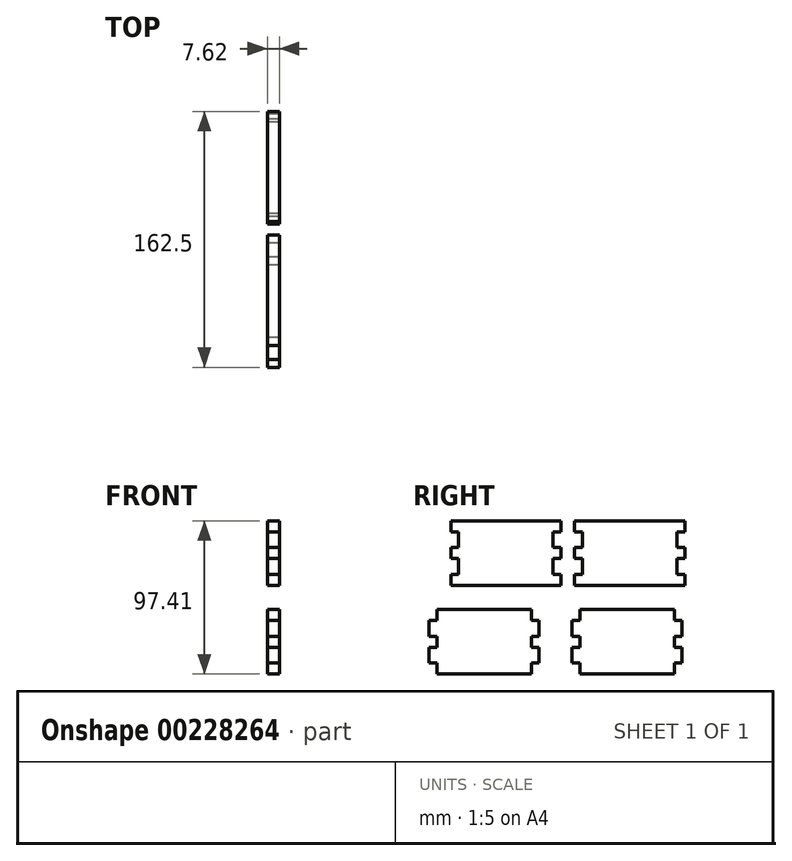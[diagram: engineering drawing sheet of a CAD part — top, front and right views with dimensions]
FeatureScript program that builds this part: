
annotation { "Feature Type Name" : "Feature", "Feature Type Description" : "" }
export const myFeature = defineFeature(function(context is Context, id is Id, definition is map)
    precondition{}
    {
        {
            var Q0;
            Q0=qCreatedBy(makeId("Right.planeOp"),FACE);
            var sketch = newSketch(context, id + "F0", { "sketchPlane" : qUnion([Q0])});
            skLineSegment(sketch, "E0", {"start": v(17.1, 53.44) * mm, "end": v(-52.9, 53.44) * mm});
            skLineSegment(sketch, "E1", {"start": v(-52.9, 53.44) * mm, "end": v(-52.9, 46.44) * mm});
            skLineSegment(sketch, "E2", {"start": v(-52.9, 46.44) * mm, "end": v(-47.9, 46.44) * mm});
            skLineSegment(sketch, "E3", {"start": v(-47.9, 46.44) * mm, "end": v(-47.9, 36.44) * mm});
            skLineSegment(sketch, "E4", {"start": v(-47.9, 36.44) * mm, "end": v(-52.9, 36.44) * mm});
            skLineSegment(sketch, "E5", {"start": v(-52.9, 36.44) * mm, "end": v(-52.9, 29.44) * mm});
            skLineSegment(sketch, "E6", {"start": v(-52.9, 29.44) * mm, "end": v(-47.9, 29.44) * mm});
            skLineSegment(sketch, "E7", {"start": v(-47.9, 29.44) * mm, "end": v(-47.9, 19.44) * mm});
            skLineSegment(sketch, "E8", {"start": v(-47.9, 19.44) * mm, "end": v(-52.9, 19.44) * mm});
            skLineSegment(sketch, "E9", {"start": v(-52.9, 19.44) * mm, "end": v(-52.9, 12.44) * mm});
            skLineSegment(sketch, "E10", {"start": v(-52.9, 12.44) * mm, "end": v(17.1, 12.44) * mm});
            skLineSegment(sketch, "E11", {"start": v(17.1, 12.44) * mm, "end": v(17.1, 19.44) * mm});
            skLineSegment(sketch, "E12", {"start": v(17.1, 19.44) * mm, "end": v(12.1, 19.44) * mm});
            skLineSegment(sketch, "E13", {"start": v(12.1, 19.44) * mm, "end": v(12.1, 29.44) * mm});
            skLineSegment(sketch, "E14", {"start": v(12.1, 29.44) * mm, "end": v(17.1, 29.44) * mm});
            skLineSegment(sketch, "E15", {"start": v(17.1, 29.44) * mm, "end": v(17.1, 36.44) * mm});
            skLineSegment(sketch, "E16", {"start": v(17.1, 36.44) * mm, "end": v(12.1, 36.44) * mm});
            skLineSegment(sketch, "E17", {"start": v(12.1, 36.44) * mm, "end": v(12.1, 46.44) * mm});
            skLineSegment(sketch, "E18", {"start": v(12.1, 46.44) * mm, "end": v(17.1, 46.44) * mm});
            skLineSegment(sketch, "E19", {"start": v(17.1, 46.44) * mm, "end": v(17.1, 53.44) * mm});
            skLineSegment(sketch, "E20.MirrorCS", {"start": v(25.75, 36.44) * mm, "end": v(30.75, 36.44) * mm});
            skLineSegment(sketch, "E21.MirrorCS", {"start": v(95.75, 29.44) * mm, "end": v(90.75, 29.44) * mm});
            skLineSegment(sketch, "E22.MirrorCS", {"start": v(30.75, 46.44) * mm, "end": v(25.75, 46.44) * mm});
            skLineSegment(sketch, "E23.MirrorCS", {"start": v(90.75, 19.44) * mm, "end": v(95.75, 19.44) * mm});
            skLineSegment(sketch, "E24.MirrorCS", {"start": v(95.75, 46.44) * mm, "end": v(90.75, 46.44) * mm});
            skLineSegment(sketch, "E25.MirrorCS", {"start": v(25.75, 19.44) * mm, "end": v(30.75, 19.44) * mm});
            skLineSegment(sketch, "E26.MirrorCS", {"start": v(30.75, 29.44) * mm, "end": v(25.75, 29.44) * mm});
            skLineSegment(sketch, "E27.MirrorCS", {"start": v(90.75, 36.44) * mm, "end": v(95.75, 36.44) * mm});
            skLineSegment(sketch, "E28.MirrorCS", {"start": v(30.75, 19.44) * mm, "end": v(30.75, 29.44) * mm});
            skLineSegment(sketch, "E29.MirrorCS", {"start": v(90.75, 29.44) * mm, "end": v(90.75, 19.44) * mm});
            skLineSegment(sketch, "E30.MirrorCS", {"start": v(95.75, 36.44) * mm, "end": v(95.75, 29.44) * mm});
            skLineSegment(sketch, "E31.MirrorCS", {"start": v(95.75, 19.44) * mm, "end": v(95.75, 12.44) * mm});
            skLineSegment(sketch, "E32.MirrorCS", {"start": v(95.75, 53.44) * mm, "end": v(95.75, 46.44) * mm});
            skLineSegment(sketch, "E33.MirrorCS", {"start": v(95.75, 12.44) * mm, "end": v(25.75, 12.44) * mm});
            skLineSegment(sketch, "E34.MirrorCS", {"start": v(25.75, 12.44) * mm, "end": v(25.75, 19.44) * mm});
            skLineSegment(sketch, "E35.MirrorCS", {"start": v(25.75, 53.44) * mm, "end": v(95.75, 53.44) * mm});
            skLineSegment(sketch, "E36.MirrorCS", {"start": v(25.75, 29.44) * mm, "end": v(25.75, 36.44) * mm});
            skLineSegment(sketch, "E37.MirrorCS", {"start": v(30.75, 36.44) * mm, "end": v(30.75, 46.44) * mm});
            skLineSegment(sketch, "E38.MirrorCS", {"start": v(25.75, 46.44) * mm, "end": v(25.75, 53.44) * mm});
            skLineSegment(sketch, "E39.MirrorCS", {"start": v(90.75, 46.44) * mm, "end": v(90.75, 36.44) * mm});
            skLineSegment(sketch, "E40", {"start": v(-61.75, -2.97) * mm, "end": v(-1.75, -2.97) * mm});
            skLineSegment(sketch, "E41", {"start": v(-61.75, -2.97) * mm, "end": v(-61.75, -9.97) * mm});
            skLineSegment(sketch, "E42", {"start": v(-61.75, -9.97) * mm, "end": v(-66.75, -9.97) * mm});
            skLineSegment(sketch, "E43", {"start": v(-66.75, -9.97) * mm, "end": v(-66.75, -19.97) * mm});
            skLineSegment(sketch, "E44", {"start": v(-66.75, -19.97) * mm, "end": v(-61.75, -19.97) * mm});
            skLineSegment(sketch, "E45", {"start": v(-61.75, -19.97) * mm, "end": v(-61.75, -26.97) * mm});
            skLineSegment(sketch, "E46", {"start": v(-61.75, -26.97) * mm, "end": v(-66.75, -26.97) * mm});
            skLineSegment(sketch, "E47", {"start": v(-66.75, -26.97) * mm, "end": v(-66.75, -36.97) * mm});
            skLineSegment(sketch, "E48", {"start": v(-66.75, -36.97) * mm, "end": v(-61.75, -36.97) * mm});
            skPoint(sketch, "E48.endSnap0", {"position": v(-61.75, -23.47) * mm});
            skLineSegment(sketch, "E49", {"start": v(-61.75, -36.97) * mm, "end": v(-61.75, -43.97) * mm});
            skLineSegment(sketch, "E50", {"start": v(-61.75, -43.97) * mm, "end": v(-1.75, -43.97) * mm});
            skLineSegment(sketch, "E51", {"start": v(-1.75, -2.97) * mm, "end": v(-1.75, -9.97) * mm});
            skLineSegment(sketch, "E52", {"start": v(-1.75, -9.97) * mm, "end": v(3.25, -9.97) * mm});
            skLineSegment(sketch, "E53", {"start": v(3.25, -9.97) * mm, "end": v(3.25, -19.97) * mm});
            skLineSegment(sketch, "E54", {"start": v(3.25, -19.97) * mm, "end": v(-1.75, -19.97) * mm});
            skLineSegment(sketch, "E55", {"start": v(-1.75, -19.97) * mm, "end": v(-1.75, -26.97) * mm});
            skLineSegment(sketch, "E56", {"start": v(-1.75, -26.97) * mm, "end": v(3.25, -26.97) * mm});
            skLineSegment(sketch, "E57", {"start": v(3.25, -26.97) * mm, "end": v(3.25, -36.97) * mm});
            skLineSegment(sketch, "E58", {"start": v(3.25, -36.97) * mm, "end": v(-1.75, -36.97) * mm});
            skLineSegment(sketch, "E59", {"start": v(-1.75, -43.97) * mm, "end": v(-1.75, -36.97) * mm});
            skLineSegment(sketch, "E60.MirrorCS", {"start": v(89.08, -2.97) * mm, "end": v(29.08, -2.97) * mm});
            skLineSegment(sketch, "E61.MirrorCS", {"start": v(89.08, -2.97) * mm, "end": v(89.08, -9.97) * mm});
            skLineSegment(sketch, "E62.MirrorCS", {"start": v(29.08, -2.97) * mm, "end": v(29.08, -9.97) * mm});
            skLineSegment(sketch, "E63.MirrorCS", {"start": v(29.08, -9.97) * mm, "end": v(24.08, -9.97) * mm});
            skLineSegment(sketch, "E64.MirrorCS", {"start": v(24.08, -9.97) * mm, "end": v(24.08, -19.97) * mm});
            skLineSegment(sketch, "E65.MirrorCS", {"start": v(24.08, -19.97) * mm, "end": v(29.08, -19.97) * mm});
            skLineSegment(sketch, "E66.MirrorCS", {"start": v(29.08, -26.97) * mm, "end": v(24.08, -26.97) * mm});
            skLineSegment(sketch, "E67.MirrorCS", {"start": v(24.08, -26.97) * mm, "end": v(24.08, -36.97) * mm});
            skLineSegment(sketch, "E68.MirrorCS", {"start": v(24.08, -36.97) * mm, "end": v(29.08, -36.97) * mm});
            skLineSegment(sketch, "E69.MirrorCS", {"start": v(29.08, -43.97) * mm, "end": v(29.08, -36.97) * mm});
            skLineSegment(sketch, "E70.MirrorCS", {"start": v(89.08, -43.97) * mm, "end": v(29.08, -43.97) * mm});
            skLineSegment(sketch, "E71.MirrorCS", {"start": v(89.08, -36.97) * mm, "end": v(89.08, -43.97) * mm});
            skLineSegment(sketch, "E72.MirrorCS", {"start": v(94.08, -36.97) * mm, "end": v(89.08, -36.97) * mm});
            skLineSegment(sketch, "E73.MirrorCS", {"start": v(94.08, -26.97) * mm, "end": v(94.08, -36.97) * mm});
            skLineSegment(sketch, "E74.MirrorCS", {"start": v(89.08, -26.97) * mm, "end": v(94.08, -26.97) * mm});
            skLineSegment(sketch, "E75.MirrorCS", {"start": v(89.08, -19.97) * mm, "end": v(89.08, -26.97) * mm});
            skLineSegment(sketch, "E76.MirrorCS", {"start": v(94.08, -9.97) * mm, "end": v(94.08, -19.97) * mm});
            skLineSegment(sketch, "E77", {"start": v(29.08, -19.97) * mm, "end": v(29.08, -26.97) * mm});
            skLineSegment(sketch, "E78", {"start": v(89.08, -19.97) * mm, "end": v(94.08, -19.97) * mm});
            skLineSegment(sketch, "E79", {"start": v(94.08, -9.97) * mm, "end": v(89.08, -9.97) * mm});
            skSolve(sketch);
        }
        {
            var Q0;
            Q0=qCreatedBy(makeId("Right.planeOp"),FACE);
            var sketch = newSketch(context, id + "F1", { "sketchPlane" : qUnion([Q0])});
            skSolve(sketch);
        }
        {
            var Q0;
            Q0=makeQuery(id+"F0.imprint","IMPRINT",FACE,{"disambiguationData":[TD([[makeQuery(id+"F0.imprint","IMPRINT",EDGE,{"derivedFrom":sQuery(id+"F0.wireOp",EDGE,"E40")}),-1.0]])]});
            extrude(context, id + "F2", {"entities" : qUnion([Q0]), "depth" : 6.1 * mm});
        }
        {
            var Q0;
            Q0 = qSketchRegion(id + "F0", true);
            var Q1;
            Q1 = qSketchRegion(id + "F1", true);
            extrude(context, id + "F3", {"entities" : qUnion([Q0, Q1]), "operationType" : NewBodyOperationType.ADD, "depth" : 7.62 * mm});
        }
    });
